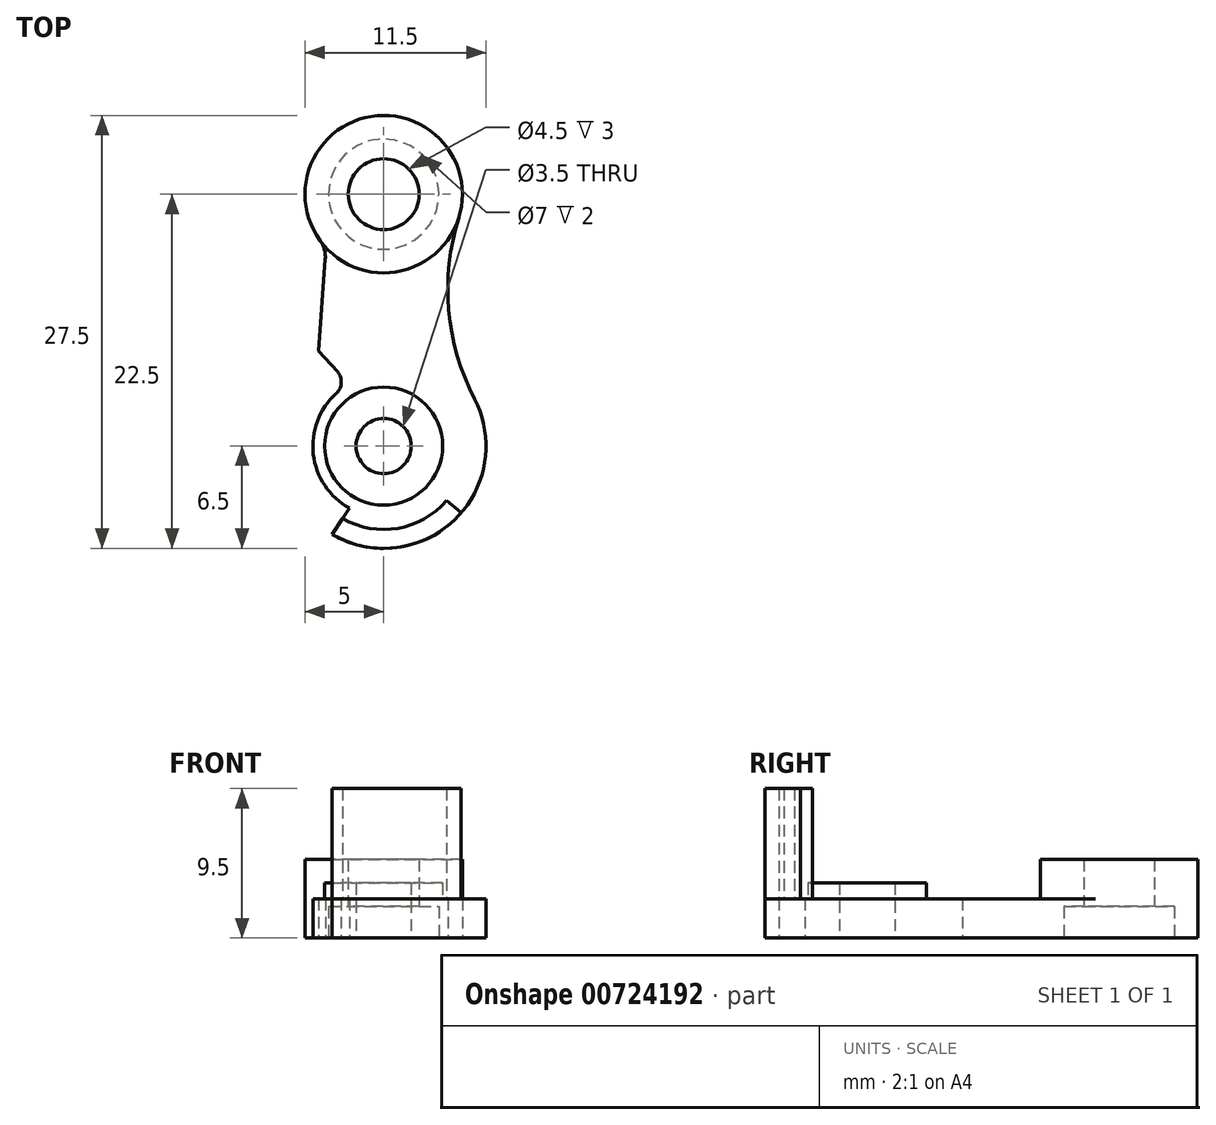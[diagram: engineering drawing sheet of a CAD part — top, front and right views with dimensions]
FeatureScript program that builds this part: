
annotation { "Feature Type Name" : "Feature", "Feature Type Description" : "" }
export const myFeature = defineFeature(function(context is Context, id is Id, definition is map)
    precondition{}
    {
        {
            var Q0;
            Q0=qCreatedBy(makeId("Top.planeOp"),FACE);
            var sketch = newSketch(context, id + "F0", { "sketchPlane" : qUnion([Q0])});
            skArc(sketch, "E0", {"start": v(4.77, -1.5) * mm, "mid": v(-0.81, 4.93) * mm, "end": v(-4.04, -2.94) * mm});
            skCircle(sketch, "E1", {"center": v(0, 0) * mm, "radius": 2.25 * mm});
            skArc(sketch, "E2", {"start": v(-3.27, -21.62) * mm, "mid": v(4.48, -20.7) * mm, "end": v(5.77, -13.01) * mm});
            skArc(sketch, "E3", {"start": v(-3.02, -12.66) * mm, "mid": v(-4.47, -16.52) * mm, "end": v(-2.17, -19.94) * mm});
            skArc(sketch, "E4", {"start": v(4.77, -1.5) * mm, "mid": v(4.13, -7.35) * mm, "end": v(5.77, -13.01) * mm});
            skLineSegment(sketch, "E5", {"start": v(-3.7, -4.1) * mm, "end": v(-4.13, -9.96) * mm});
            skLineSegment(sketch, "E6", {"start": v(-4.13, -9.96) * mm, "end": v(-2.95, -11.27) * mm});
            skArc(sketch, "E7", {"start": v(-3.7, -4.1) * mm, "mid": v(-3.77, -3.5) * mm, "end": v(-4.04, -2.94) * mm});
            skArc(sketch, "E8", {"start": v(-3.02, -12.66) * mm, "mid": v(-2.7, -11.98) * mm, "end": v(-2.95, -11.27) * mm});
            skCircle(sketch, "E9", {"center": v(0, -16) * mm, "radius": 1.75 * mm});
            skLineSegment(sketch, "E10", {"start": v(-2.17, -19.94) * mm, "end": v(-3.27, -21.62) * mm});
            skSolve(sketch);
        }
        {
            var Q0;
            Q0=makeQuery(id+"F0.imprint","IMPRINT",FACE,{"disambiguationData":[TD([[makeQuery(id+"F0.imprint","IMPRINT",EDGE,{"derivedFrom":sQuery(id+"F0.wireOp",EDGE,"E0")}),1.0]])]});
            extrude(context, id + "F1", {"entities" : qUnion([Q0]), "depth" : 2.5 * mm, "offsetDistance" : 25 * mm});
        }
        {
            var Q0;
            Q0=makeQuery(id+"F1.opExtrude","CAP_FACE",FACE,{"disambiguationData":[OSD([sQuery(id+"F0.wireOp",EDGE,"E0"),sQuery(id+"F0.wireOp",EDGE,"E1"),sQuery(id+"F0.wireOp",EDGE,"E2"),sQuery(id+"F0.wireOp",EDGE,"E3"),sQuery(id+"F0.wireOp",EDGE,"E4"),sQuery(id+"F0.wireOp",EDGE,"E5"),sQuery(id+"F0.wireOp",EDGE,"E6"),sQuery(id+"F0.wireOp",EDGE,"GXQV9pzC-pBOt-UUZr-pORs-scLMkWEZ16K3"),sQuery(id+"F0.wireOp",EDGE,"E7")])],"isStart":false});
            var sketch = newSketch(context, id + "F2", { "sketchPlane" : qUnion([Q0])});
            skCircle(sketch, "E11", {"center": v(0, 0) * mm, "radius": 2.25 * mm});
            skCircle(sketch, "E12", {"center": v(0, 0) * mm, "radius": 5 * mm});
            skSolve(sketch);
        }
        {
            var Q0;
            Q0=makeQuery(id+"F2.imprint","IMPRINT",FACE,{"disambiguationData":[TD([[makeQuery(id+"F2.imprint","IMPRINT",EDGE,{"derivedFrom":sQuery(id+"F2.wireOp",EDGE,"E11")}),-1.0]])]});
            extrude(context, id + "F3", {"entities" : qUnion([Q0]), "operationType" : NewBodyOperationType.ADD, "depth" : 2.5 * mm, "offsetDistance" : 25 * mm});
        }
        {
            var Q0;
            Q0=makeQuery(id+"F1.opExtrude","CAP_FACE",FACE,{"disambiguationData":[OSD([sQuery(id+"F0.wireOp",EDGE,"E0"),sQuery(id+"F0.wireOp",EDGE,"E1"),sQuery(id+"F0.wireOp",EDGE,"E2"),sQuery(id+"F0.wireOp",EDGE,"E3"),sQuery(id+"F0.wireOp",EDGE,"E4"),sQuery(id+"F0.wireOp",EDGE,"E5"),sQuery(id+"F0.wireOp",EDGE,"E6"),sQuery(id+"F0.wireOp",EDGE,"E7"),sQuery(id+"F0.wireOp",EDGE,"E8"),sQuery(id+"F0.wireOp",EDGE,"E9"),sQuery(id+"F0.wireOp",EDGE,"E10")])],"isStart":false});
            var sketch = newSketch(context, id + "F4", { "sketchPlane" : qUnion([Q0])});
            skCircle(sketch, "E13", {"center": v(0, -16) * mm, "radius": 1.75 * mm});
            skCircle(sketch, "E14", {"center": v(0, -16) * mm, "radius": 3.75 * mm});
            skSolve(sketch);
        }
        {
            var Q0;
            Q0 = qSketchRegion(id + "F4", true);
            extrude(context, id + "F5", {"entities" : qUnion([Q0]), "operationType" : NewBodyOperationType.ADD, "depth" : 1 * mm, "offsetDistance" : 25 * mm});
        }
        {
            var Q0;
            Q0=makeQuery(id+"F1.opExtrude","CAP_FACE",FACE,{"disambiguationData":[OSD([sQuery(id+"F0.wireOp",EDGE,"E0"),sQuery(id+"F0.wireOp",EDGE,"E1"),sQuery(id+"F0.wireOp",EDGE,"E2"),sQuery(id+"F0.wireOp",EDGE,"E3"),sQuery(id+"F0.wireOp",EDGE,"E4"),sQuery(id+"F0.wireOp",EDGE,"E5"),sQuery(id+"F0.wireOp",EDGE,"E6"),sQuery(id+"F0.wireOp",EDGE,"E7"),sQuery(id+"F0.wireOp",EDGE,"E8"),sQuery(id+"F0.wireOp",EDGE,"E9"),sQuery(id+"F0.wireOp",EDGE,"E10")])],"isStart":false});
            var sketch = newSketch(context, id + "F6", { "sketchPlane" : qUnion([Q0])});
            skSolve(sketch);
        }
        {
            var Q0;
            Q0=makeQuery(id+"F6.imprint","IMPRINT",FACE,{"disambiguationData":[TD([[makeQuery(id+"F6.imprint","IMPRINT",EDGE,{"derivedFrom":makeQuery(id+"F1.opExtrude","CAP_EDGE",EDGE,{"disambiguationData":[OSD([sQuery(id+"F0.wireOp",EDGE,"E2")])],"isStart":false})}),1.0]])]});
            var sketch = newSketch(context, id + "F7", { "sketchPlane" : qUnion([Q0])});
            skArc(sketch, "E15", {"start": v(-3.26, -21.61) * mm, "mid": v(1.08, -22.4) * mm, "end": v(4.91, -20.23) * mm});
            skArc(sketch, "E16", {"start": v(-2.6, -20.6) * mm, "mid": v(0.9, -21.22) * mm, "end": v(3.99, -19.46) * mm});
            skLineSegment(sketch, "E17", {"start": v(-2.6, -20.6) * mm, "end": v(-3.26, -21.61) * mm});
            skLineSegment(sketch, "E18", {"start": v(3.99, -19.46) * mm, "end": v(4.91, -20.23) * mm});
            skSolve(sketch);
        }
        {
            var Q0;
            Q0 = qSketchRegion(id + "F7", true);
            extrude(context, id + "F8", {"entities" : qUnion([Q0]), "operationType" : NewBodyOperationType.ADD, "depth" : 7 * mm, "offsetDistance" : 25 * mm});
        }
        {
            var Q0;
            Q0=makeQuery(id+"F1.opExtrude","CAP_FACE",FACE,{"disambiguationData":[OSD([sQuery(id+"F0.wireOp",EDGE,"E0"),sQuery(id+"F0.wireOp",EDGE,"E1"),sQuery(id+"F0.wireOp",EDGE,"E2"),sQuery(id+"F0.wireOp",EDGE,"E3"),sQuery(id+"F0.wireOp",EDGE,"E4"),sQuery(id+"F0.wireOp",EDGE,"E5"),sQuery(id+"F0.wireOp",EDGE,"E6"),sQuery(id+"F0.wireOp",EDGE,"E7"),sQuery(id+"F0.wireOp",EDGE,"E8"),sQuery(id+"F0.wireOp",EDGE,"E9"),sQuery(id+"F0.wireOp",EDGE,"E10")])],"isStart":true});
            var sketch = newSketch(context, id + "F9", { "sketchPlane" : qUnion([Q0])});
            skCircle(sketch, "E19", {"center": v(0, 0) * mm, "radius": 3.5 * mm});
            skSolve(sketch);
        }
        {
            var Q0;
            Q0=makeQuery(id+"F9.imprint","IMPRINT",FACE,{"disambiguationData":[TD([[makeQuery(id+"F9.imprint","IMPRINT",EDGE,{"derivedFrom":sQuery(id+"F9.wireOp",EDGE,"E19")}),1.0]])]});
            extrude(context, id + "F10", {"entities" : qUnion([Q0]), "operationType" : NewBodyOperationType.REMOVE, "oppositeDirection" : true, "depth" : 2 * mm, "offsetDistance" : 25 * mm});
        }
    });
